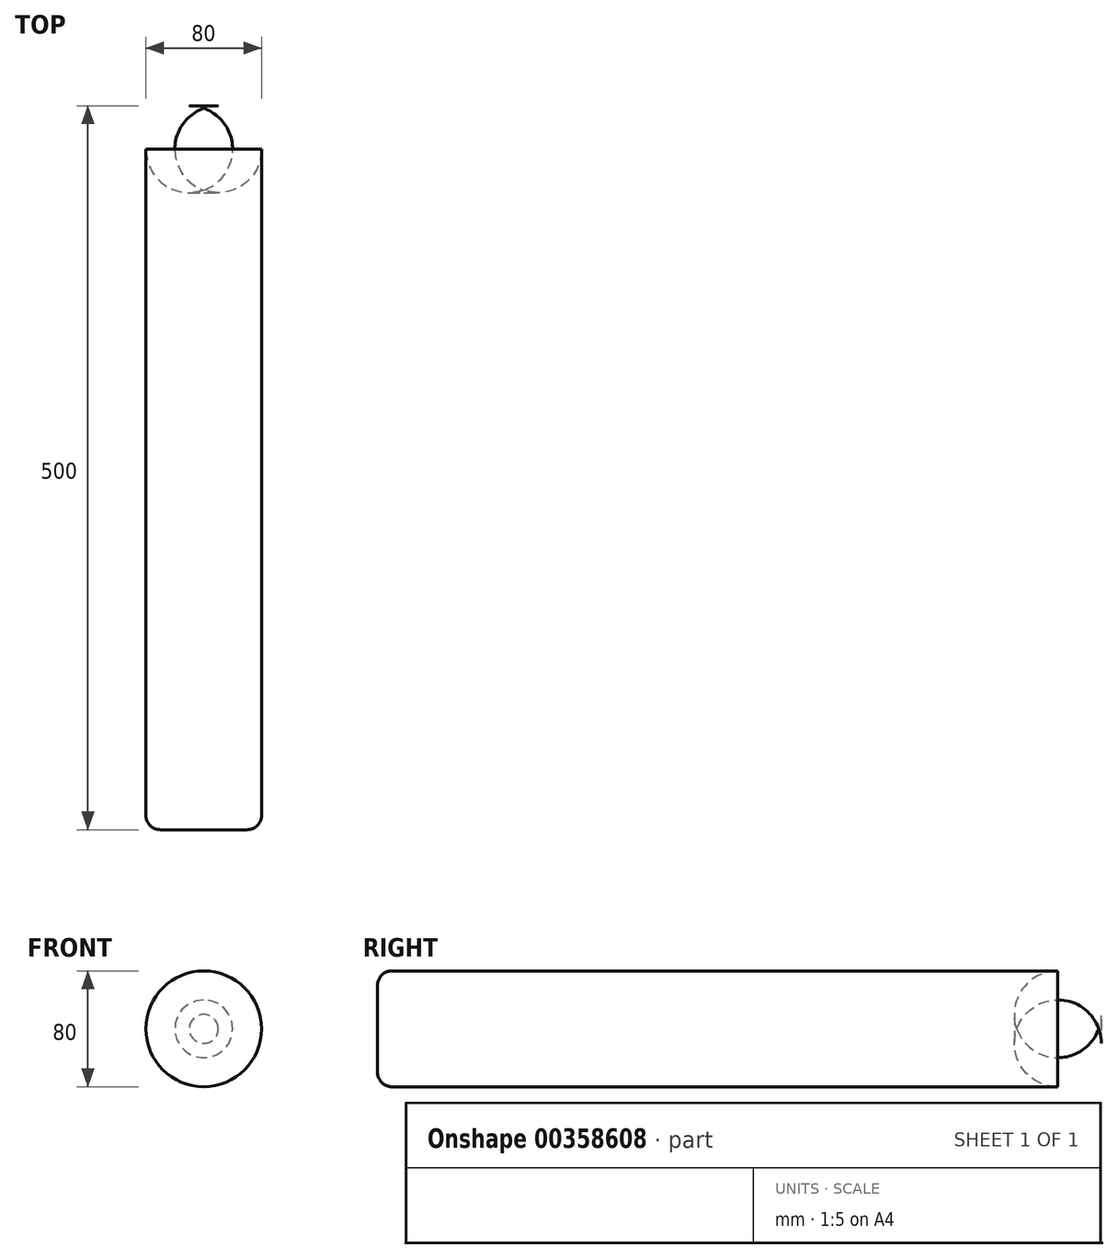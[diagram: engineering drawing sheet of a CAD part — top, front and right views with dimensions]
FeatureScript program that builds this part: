
annotation { "Feature Type Name" : "Feature", "Feature Type Description" : "" }
export const myFeature = defineFeature(function(context is Context, id is Id, definition is map)
    precondition{}
    {
        {
            var Q0;
            Q0=qCreatedBy(makeId("Front.planeOp"),FACE);
            var sketch = newSketch(context, id + "F0", { "sketchPlane" : qUnion([Q0])});
            skCircle(sketch, "E0", {"center": v(0, 0) * mm, "radius": 40 * mm});
            skSolve(sketch);
        }
        {
            var Q0;
            Q0 = qSketchRegion(id + "F0", true);
            extrude(context, id + "F1", {"entities" : qUnion([Q0]), "oppositeDirection" : true, "depth" : 500 * mm});
        }
        {
            var Q0;
            Q0=makeQuery(id+"F1.opExtrude","CAP_EDGE",EDGE,{"disambiguationData":[OSD([sQuery(id+"F0.wireOp",EDGE,"E0")])],"isStart":false});
            fillet(context, id + "F2", {"entities" : qUnion([Q0]), "radius" : 30 * mm, "tangentPropagation" : true, "allowEdgeOverflow" : false});
        }
        {
            var Q0;
            Q0=makeQuery(id+"F1.opExtrude","CAP_EDGE",EDGE,{"disambiguationData":[OSD([sQuery(id+"F0.wireOp",EDGE,"E0")])],"isStart":true});
            fillet(context, id + "F3", {"entities" : qUnion([Q0]), "radius" : 10 * mm, "tangentPropagation" : true, "allowEdgeOverflow" : false});
        }
    });
